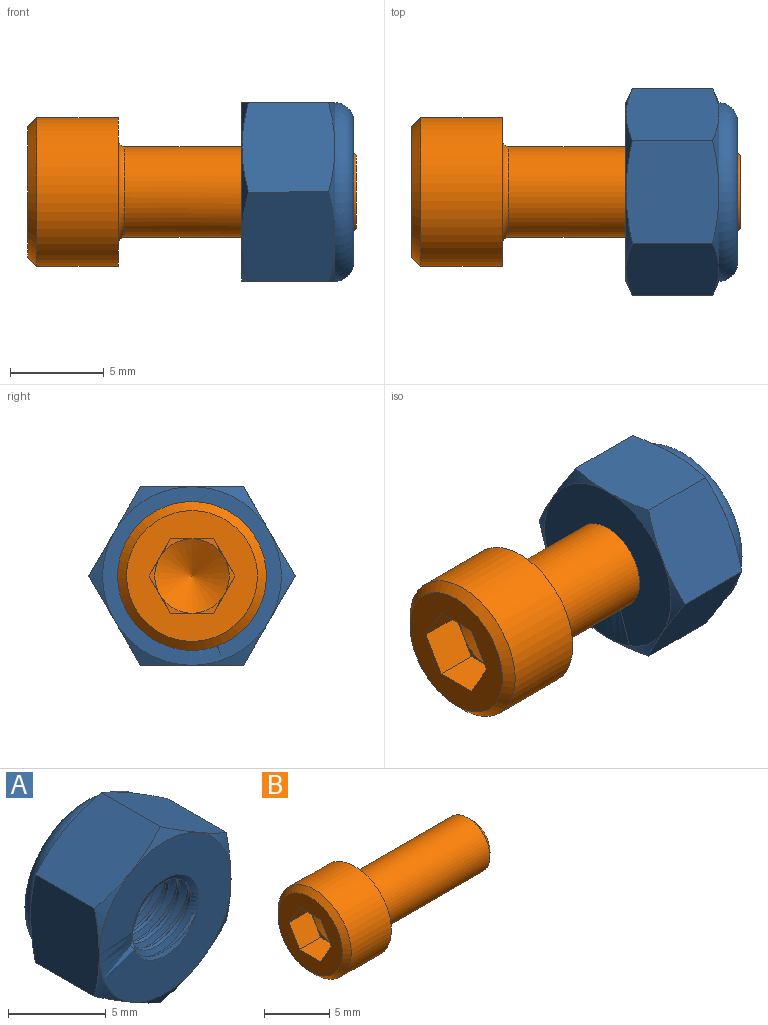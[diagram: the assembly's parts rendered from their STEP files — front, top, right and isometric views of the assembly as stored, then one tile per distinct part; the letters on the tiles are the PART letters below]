
ASSEMBLY  parts=2 mates=1
PART A: 56 faces, bbox 11.6x6.6x11.6 mm
  f0: plane 7.54x7.54mm, normal (0,1,0), area 18.1mm2, adj f1,f55
  f1: cylinder r=2.91mm len=5.82mm, axis (0,-1,0), area 2.8mm2, adj f0,f2
  f2: plane 7.54x7.54mm, normal (0,-1,0), area 18.1mm2, adj f1,f3
  f3: torus R=3.77mm, axis (0,-1,0), area 35.7mm2, adj f2,f4
  f4: plane 9.78x9.78mm, normal (0,1,0), area 50.6mm2, adj f3,f5,f6,f52,f53,f54
  f5: cone r=2.52mm half-angle=60deg, axis (0,0.99,0.16), area 0mm2, adj f4,f54
  f6: cone r=2.52mm half-angle=60deg, axis (0,0.99,0.16), area 5.9mm2, adj f4,f7,f52
  f7: cylinder r=2.09mm len=4.18mm, axis (0,0.99,0.16), area 2.6mm2, adj f6,f8
  f8: cone r=2.09mm half-angle=60deg, axis (0,-0.99,-0.16), area 5.7mm2, adj f7,f9
  f9: cylinder r=2.41mm len=4.83mm, axis (0,-1,0), area 2.7mm2, adj f8,f10
  f10: cone r=2.52mm half-angle=60deg, axis (0,0.99,0.16), area 5.6mm2, adj f9,f11
  f11: cylinder r=2.09mm len=4.18mm, axis (0,0.99,0.16), area 2.6mm2, adj f10,f12
  f12: cone r=2.09mm half-angle=60deg, axis (0,-0.99,-0.16), area 5.7mm2, adj f11,f13
  f13: cylinder r=2.41mm len=4.83mm, axis (0,-1,0), area 2.7mm2, adj f12,f14
  f14: cone r=2.52mm half-angle=60deg, axis (0,0.99,0.16), area 5.6mm2, adj f13,f15
  f15: cylinder r=2.09mm len=4.18mm, axis (0,0.99,0.16), area 2.6mm2, adj f14,f16
  f16: cone r=2.09mm half-angle=60deg, axis (0,-0.99,-0.16), area 5.7mm2, adj f15,f17
  f17: cylinder r=2.41mm len=4.83mm, axis (0,-1,0), area 2.7mm2, adj f16,f18
  f18: cone r=2.52mm half-angle=60deg, axis (0,0.99,0.16), area 5.6mm2, adj f17,f19
  f19: cylinder r=2.09mm len=4.18mm, axis (0,0.99,0.16), area 2.6mm2, adj f18,f20
  f20: cone r=2.09mm half-angle=60deg, axis (0,-0.99,-0.16), area 5.7mm2, adj f19,f21
  f21: cylinder r=2.41mm len=4.83mm, axis (0,-1,0), area 2.7mm2, adj f20,f22
  f22: cone r=2.52mm half-angle=60deg, axis (0,0.99,0.16), area 5.6mm2, adj f21,f23
  f23: cylinder r=2.09mm len=4.18mm, axis (0,0.99,0.16), area 2.6mm2, adj f22,f24
  f24: cone r=2.09mm half-angle=60deg, axis (0,-0.99,-0.16), area 5.7mm2, adj f23,f25
  f25: cylinder r=2.41mm len=4.83mm, axis (0,-1,0), area 2.7mm2, adj f24,f26
  f26: cone r=2.52mm half-angle=60deg, axis (0,0.99,0.16), area 5.5mm2, adj f25,f27,f51
  f27: cone r=2.41mm half-angle=65deg, axis (0,-1,0), area 2.3mm2, adj f26,f28,f50,f51
  f28: plane 9.94x9.94mm, normal (0,-1,0), area 52.8mm2, adj f27,f29,f32,f45,f46,f47,f48,f49
  f29: cone r=2.41mm half-angle=65deg, axis (0,-1,0), area 0mm2, adj f28,f30
  f30: cone r=2.52mm half-angle=60deg, axis (0,0.99,0.16), area 0mm2, adj f29,f31
  f31: cylinder r=2.41mm len=4.47mm, axis (0,-1,0), area 0mm2, adj f30,f50
  f32: cone r=5.5mm half-angle=65deg, axis (0,1,0), area 2.1mm2, adj f28,f33,f44
  f33: plane 5.39x5.19mm, normal (0.5,0,0.87), area 26mm2, adj f32,f34,f42,f43,f44,f49
  f34: plane 5.39x5.19mm, normal (-0.5,0,0.87), area 26mm2, adj f33,f35,f41,f42,f48,f49
  f35: plane 5.93x5.39mm, normal (-1,0,0), area 26mm2, adj f34,f36,f40,f41,f47,f48
  f36: plane 5.39x5.19mm, normal (-0.5,0,-0.87), area 26mm2, adj f35,f37,f39,f40,f46,f47
  f37: plane 5.39x5.19mm, normal (0.5,0,-0.87), area 26mm2, adj f36,f38,f39,f44,f45,f46
  f38: cone r=4.76mm half-angle=65deg, axis (0,-1,0), area 2.1mm2, adj f37,f44,f55
  f39: cone r=4.76mm half-angle=65deg, axis (0,-1,0), area 2.1mm2, adj f36,f37,f55
  f40: cone r=4.76mm half-angle=65deg, axis (0,-1,0), area 2.1mm2, adj f35,f36,f55
  f41: cone r=4.76mm half-angle=65deg, axis (0,-1,0), area 2.1mm2, adj f34,f35,f55
  f42: cone r=4.76mm half-angle=65deg, axis (0,-1,0), area 2.1mm2, adj f33,f34,f55
  f43: cone r=4.76mm half-angle=65deg, axis (0,-1,0), area 2.1mm2, adj f33,f44,f55
  f44: plane 5.93x5.39mm, normal (1,0,0), area 26mm2, adj f32,f33,f37,f38,f43,f45
  f45: cone r=5.5mm half-angle=65deg, axis (0,1,0), area 2.1mm2, adj f28,f37,f44
  f46: cone r=5.5mm half-angle=65deg, axis (0,1,0), area 2.1mm2, adj f28,f36,f37
  f47: cone r=5.5mm half-angle=65deg, axis (0,1,0), area 2.1mm2, adj f28,f35,f36
  f48: cone r=5.5mm half-angle=65deg, axis (0,1,0), area 2.1mm2, adj f28,f34,f35
  f49: cone r=5.5mm half-angle=65deg, axis (0,1,0), area 2.1mm2, adj f28,f33,f34
  f50: cone r=2.09mm half-angle=60deg, axis (0,-0.99,-0.16), area 3.1mm2, adj f27,f28,f31,f51
  f51: cylinder r=2.09mm len=4.18mm, axis (0,0.99,0.16), area 1.8mm2, adj f26,f27,f50
  f52: cylinder r=2.41mm len=4.83mm, axis (0,-1,0), area 4.7mm2, adj f4,f6,f53
  f53: cone r=2.09mm half-angle=60deg, axis (0,-0.99,-0.16), area 2.7mm2, adj f4,f52,f54
  f54: cylinder r=2.09mm len=4.14mm, axis (0,0.99,0.16), area 0.9mm2, adj f4,f5,f53
  f55: torus R=3.77mm, axis (0,-1,0), area 43.1mm2, adj f0,f38,f39,f40,f41,f42,f43
PART B: 21 faces, bbox 17.5x7.9x7.9 mm
  f0: cone r=1.99mm half-angle=60deg, axis (-1,0,0), area 14.3mm2, adj f15,f16,f17,f18,f19,f20
  f1: torus R=2.77mm, axis (1,0,0), area 8.9mm2, adj f3,f7
  f2: cone r=1.94mm half-angle=45deg, axis (-1,0,0), area 9.1mm2, adj f3,f8
  f3: cylinder r=2.41mm len=11.87mm, axis (-1,0,0), area 180mm2, adj f1,f2
  f4: cylinder r=3.97mm len=7.94mm, axis (-1,0,0), area 108.3mm2, adj f5,f7
  f5: cone r=3.49mm half-angle=45deg, axis (1,0,0), area 16mm2, adj f4,f6
  f6: plane 6.97x6.97mm, normal (-1,0,0), area 24.5mm2, adj f5,f9,f10,f11,f12,f13,f14
  f7: plane 7.94x7.94mm, normal (1,0,0), area 25.4mm2, adj f1,f4
  f8: plane 3.88x3.88mm, normal (1,0,0), area 11.8mm2, adj f2
  f9: plane 2.29x1.99mm, normal (0,-0.87,-0.5), area 5.2mm2, adj f6,f10,f14,f19,f20
  f10: plane 2.29x2.29mm, normal (0,0,-1), area 5.2mm2, adj f6,f9,f11,f15,f20
  f11: plane 2.29x1.99mm, normal (0,0.87,-0.5), area 5.2mm2, adj f6,f10,f12,f15,f16
  f12: plane 2.29x1.99mm, normal (0,0.87,0.5), area 5.2mm2, adj f6,f11,f13,f16,f17
  f13: plane 2.29x2.29mm, normal (0,0,1), area 5.2mm2, adj f6,f12,f14,f17,f18
  f14: plane 2.29x1.99mm, normal (0,-0.87,0.5), area 5.2mm2, adj f6,f9,f13,f18,f19
  f15: plane 1.72x0.99mm, normal (-1,0,0), area 0.2mm2, adj f0,f10,f11
  f16: plane 1.99x0.57mm, normal (-1,0,0), area 0.2mm2, adj f0,f11,f12
  f17: plane 1.72x0.99mm, normal (-1,0,0), area 0.2mm2, adj f0,f12,f13
  f18: plane 1.72x0.99mm, normal (-1,0,0), area 0.2mm2, adj f0,f13,f14
  f19: plane 1.99x0.57mm, normal (-1,0,0), area 0.2mm2, adj f0,f9,f14
  f20: plane 1.72x0.99mm, normal (-1,0,0), area 0.2mm2, adj f0,f9,f10
PLACE A rot(axis=(-0.58,-0.58,-0.58),120deg) t=(-0.03,3.53,3.65)mm
PLACE B t=(-11.46,3.53,3.65)mm
MATE fastened A.f27 <-> B.f0  axis (-1,0,0) through (-0.03,3.53,3.65)mm
